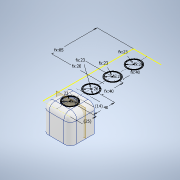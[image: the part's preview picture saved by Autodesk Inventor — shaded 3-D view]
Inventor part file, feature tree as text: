
AUTODESK INVENTOR PART (.ipt)
format: ipt  version: 2021 (Build 250183000, 183)  size: 1,751,552 bytes
history: native  units: in
note: dims shown in document units (in); Inventor stores cm internally (conversion verified against a paired STEP export)
features: extrude x10, other x9, fillet x2, sketch x1
ambient origin geometry x8: Origin, YZ Plane, XZ Plane, XY Plane, X Axis, Y Axis, Z Axis, Center Point
bodies: Body1 (feature_tree)
feature tree (22):
  extrude  "Base"  Depth=0.1969in
  other  "Top Indent Sketch"
  extrude  "Top"  Depth=0.1969in TaperAngle=0.0deg
  extrude  "Walls"  Depth=0.1969in
  fillet  "Outer"  Radius=1.0236in
  extrude  "Outer Wire"  Depth=0.1969in
  extrude  "Wall Holes"  Depth=0.1969in
  extrude  "Text"  Depth=0.1969in
  extrude  "Inner Sketch"  Depth=0.1969in
  fillet  "Inner Fillet"  Radius=1.5748in
  extrude  "Top Indent"  Depth=0.1969in TaperAngle=0.0deg
  other  "Wire Hole Plane"
  extrude  "Wire Hole"  Depth=0.1969in
  extrude  "Extrusion21"  Depth=0.1969in
  other  "Base Sketch"
  other  "Walls Sketch"
  other  "Outer Wire Sketch"
  other  "Wall Holes Sketch"
  other  "Text Sketch"
  other  "Inner Support Sketch"
  other  "Wire Hole Sketch"
  sketch  "Sketch29"  dims[d6=6.6929in d7=2.0472in d8=1.9685in d9=0.0in d10=1.0236in d11=1.0236in d12=1.0236in d13=1.0236in d14=1.5748in d15=1.5748in d16=1.5748in d19=0.7087in d20=0.0in d21=0.315in d22=0.315in d23=0.2362in d24=0.2362in d25=1.6535in d26=0.0in d27=0.9055in d28=0.9055in d29=0.9055in d30=0.9055in d31=0.7874in d32=3.3465in d33=1.5748in d35=0.9843in d36=0.4724in d38=0.3937in d39=0.0in d52=0.315in d55=0.1969in d56=0.0in d58=0.5512in d65=0.315in d66=0.1575in d67=0.1575in d68=0.315in d69=0.2774in d70=0.2774in d71=0.0499in d72=0.0499in d73=0.0787in d74=0.0in d77=0.6496in d81=0.9843in d82=0.0in d85=0.5906in d86=0.1575in d87=0.1575in d88=1.0236in d89=0.315in d90=0.1575in d92=0.0in d93=0.1181in d94=0.0in d95=0.1575in d96=0.6496in d143=0.0in d144=0.0in d158=0.0787in d159=0.0in d162=0.2362in d163=0.0in d164=0.0in d165=0.1969in d166=0.2362in d167=0.0in d168=0.1969in d169=0.1969in d170=4.7244in d171=0.0in d172=3.3465in d173=1.0236in d175=1.2992in d178=4.9213in d179=0.0in d44=0.0197in d45=0.0344in d46=0.0197in d47=0.0344in d48=0.0197in d49=0.0344in d59=0.0197in d60=0.0344in d61=0.0197in d62=0.0344in d176=0.0344in d177=0.0197in]
